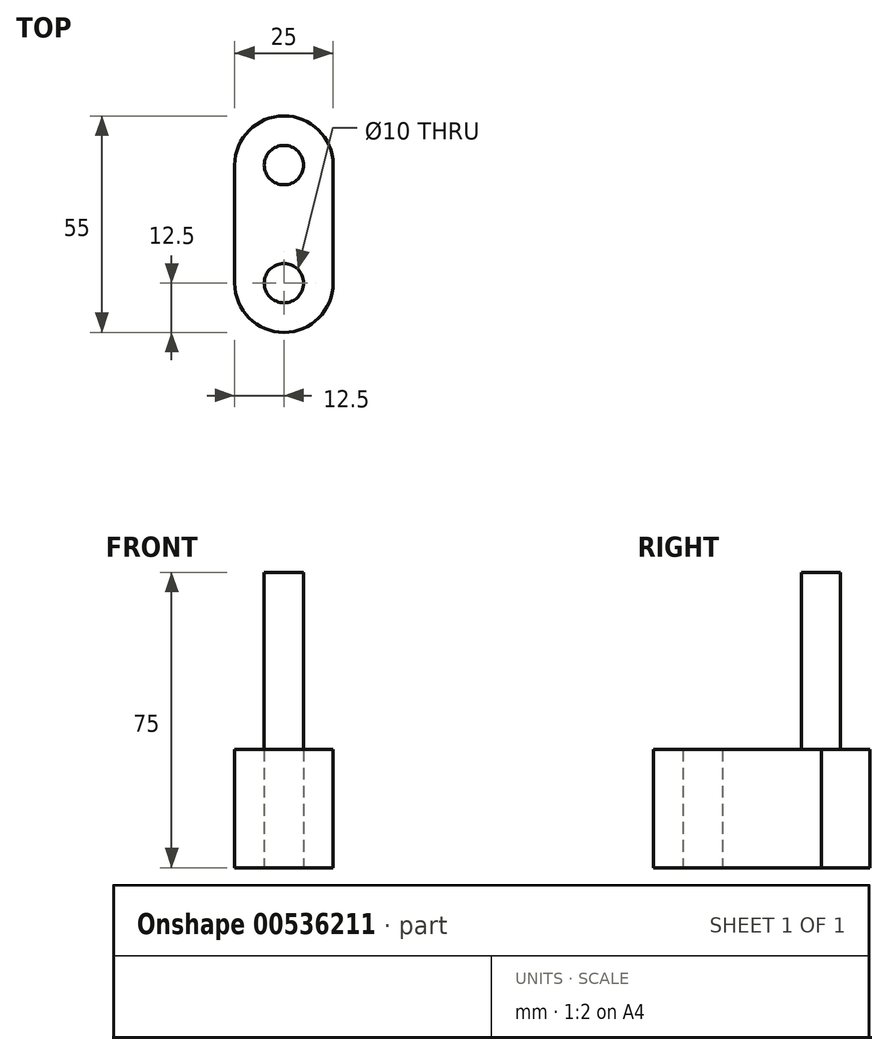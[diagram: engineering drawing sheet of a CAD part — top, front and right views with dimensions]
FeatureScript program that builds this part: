
annotation { "Feature Type Name" : "Feature", "Feature Type Description" : "" }
export const myFeature = defineFeature(function(context is Context, id is Id, definition is map)
    precondition{}
    {
        {
            var Q0;
            Q0=qCreatedBy(makeId("Top.planeOp"),FACE);
            var sketch = newSketch(context, id + "F0", { "sketchPlane" : qUnion([Q0])});
            skCircle(sketch, "E0", {"center": v(0, 0) * mm, "radius": 5 * mm});
            skLineSegment(sketch, "E1", {"start": v(0, 0) * mm, "end": v(0, 30) * mm, "construction": true});
            skCircle(sketch, "E2", {"center": v(0, 30) * mm, "radius": 5 * mm});
            skCircle(sketch, "E3", {"center": v(0, 30) * mm, "radius": 12.5 * mm});
            skCircle(sketch, "E4", {"center": v(0, 0) * mm, "radius": 12.5 * mm});
            skLineSegment(sketch, "E5", {"start": v(12.5, 30.14) * mm, "end": v(12.5, 0) * mm});
            skLineSegment(sketch, "E6", {"start": v(-12.5, 0) * mm, "end": v(-12.5, 30) * mm});
            skSolve(sketch);
        }
        {
            var Q0;
            Q0=makeQuery(id+"F0.imprint","IMPRINT",FACE,{"disambiguationData":[TD([[makeQuery(id+"F0.imprint","IMPRINT",EDGE,{"derivedFrom":sQuery(id+"F0.wireOp",EDGE,"E2")}),-1.0]])]});
            var Q1;
            Q1=makeQuery(id+"F0.imprint","IMPRINT",FACE,{"disambiguationData":[TD([[makeQuery(id+"F0.imprint","IMPRINT",EDGE,{"derivedFrom":sQuery(id+"F0.wireOp",EDGE,"E0")}),-1.0]])]});
            var Q2;
            {var subQ0=sQuery(id+"F0.wireOp",EDGE,"E6");Q2=makeQuery(id+"F0.imprint","IMPRINT",FACE,{"disambiguationData":[TD([[makeQuery(id+"F0.imprint","IMPRINT",EDGE,{"derivedFrom":subQ0}),-1.0]])]});}
            extrude(context, id + "F1", {"entities" : qUnion([Q0, Q1, Q2]), "depth" : 30 * mm, "offsetDistance" : 25 * mm});
        }
        {
            var Q0;
            Q0=makeQuery(id+"F0.imprint","IMPRINT",FACE,{"disambiguationData":[TD([[makeQuery(id+"F0.imprint","IMPRINT",EDGE,{"derivedFrom":sQuery(id+"F0.wireOp",EDGE,"E2")}),1.0]])]});
            extrude(context, id + "F2", {"entities" : qUnion([Q0]), "operationType" : NewBodyOperationType.ADD, "depth" : 75 * mm, "offsetDistance" : 25 * mm});
        }
    });
